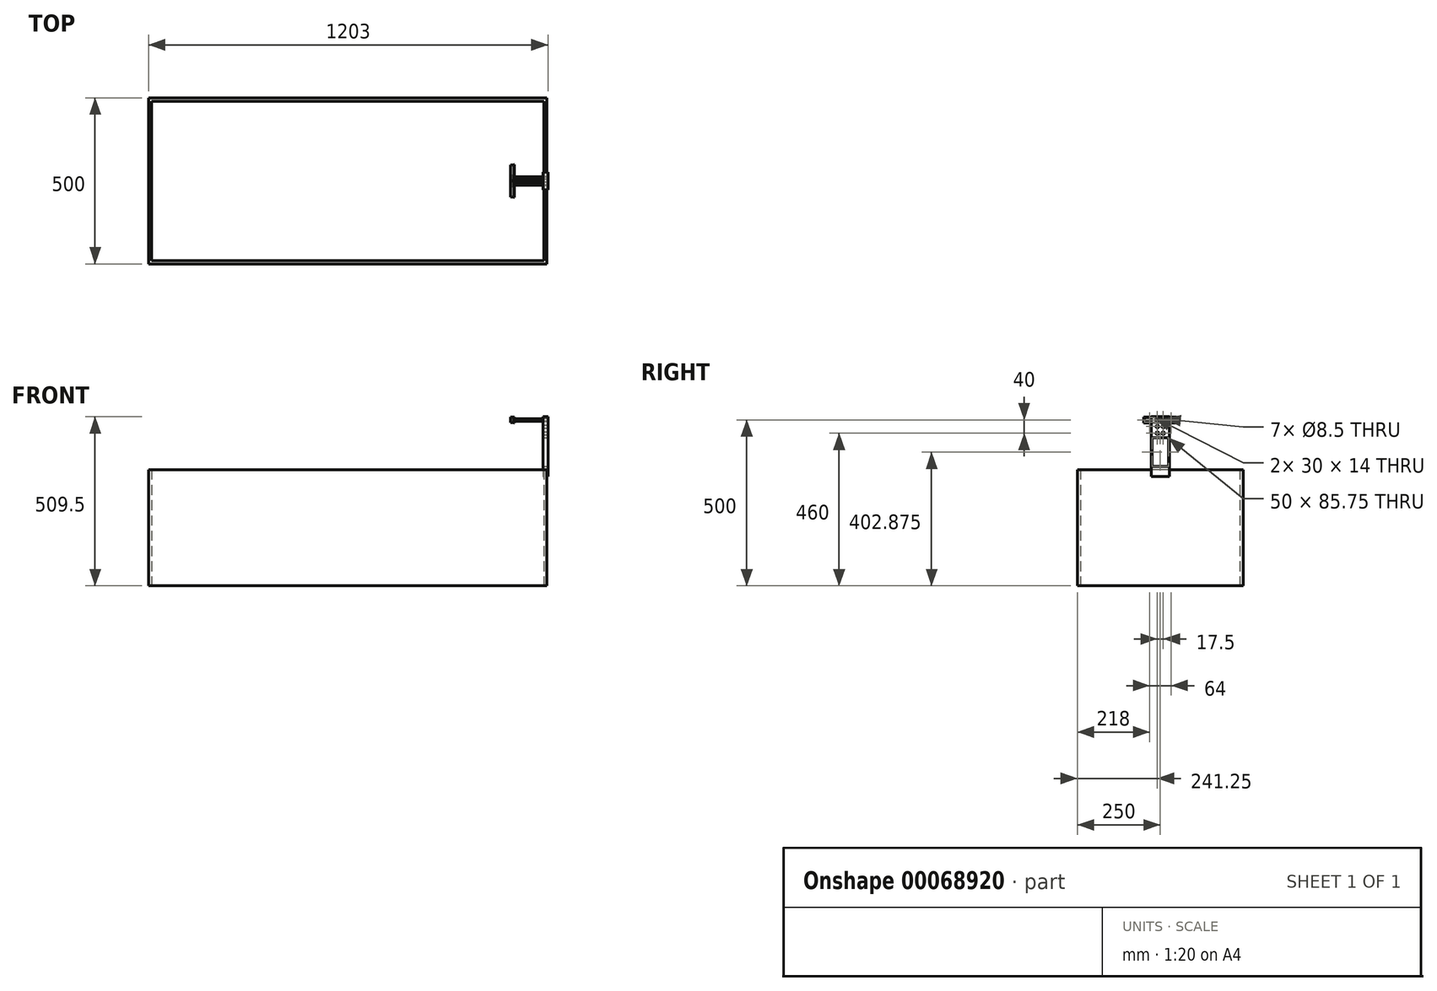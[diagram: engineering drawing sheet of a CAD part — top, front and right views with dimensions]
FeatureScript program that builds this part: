
annotation { "Feature Type Name" : "Feature", "Feature Type Description" : "" }
export const myFeature = defineFeature(function(context is Context, id is Id, definition is map)
    precondition{}
    {
        {
            var Q0;
            Q0=qCreatedBy(makeId("Right.planeOp"),FACE);
            var sketch = newSketch(context, id + "F0", { "sketchPlane" : qUnion([Q0])});
            skLineSegment(sketch, "E0.rect.bottom", {"start": v(-49.5, 9) * mm, "end": v(49.5, 9) * mm});
            skLineSegment(sketch, "E0.rect.top", {"start": v(-49.5, -9) * mm, "end": v(49.5, -9) * mm});
            skLineSegment(sketch, "E0.rect.left", {"start": v(-49.5, 9) * mm, "end": v(-49.5, -9) * mm});
            skLineSegment(sketch, "E0.rect.right", {"start": v(49.5, 9) * mm, "end": v(49.5, -9) * mm});
            skLineSegment(sketch, "E1.bottom", {"start": v(-49.5, -9) * mm, "end": v(0, -9) * mm, "construction": true});
            skLineSegment(sketch, "E1.top", {"start": v(-49.5, 9) * mm, "end": v(0, 9) * mm, "construction": true});
            skLineSegment(sketch, "E2", {"start": v(0, 9) * mm, "end": v(0, -9) * mm, "construction": true});
            skPoint(sketch, "E3.middle", {"position": v(0, 0) * mm});
            skLineSegment(sketch, "E4.bottom", {"start": v(-48, 8) * mm, "end": v(-16, 8) * mm});
            skLineSegment(sketch, "E4.top", {"start": v(-48, -8) * mm, "end": v(-16, -8) * mm});
            skLineSegment(sketch, "E4.left", {"start": v(-48, 8) * mm, "end": v(-48, -8) * mm});
            skLineSegment(sketch, "E5.MirrorCS", {"start": v(48, 8) * mm, "end": v(48, -8) * mm});
            skLineSegment(sketch, "E6.MirrorCS", {"start": v(48, 8) * mm, "end": v(16, 8) * mm});
            skLineSegment(sketch, "E7.MirrorCS", {"start": v(48, -8) * mm, "end": v(16, -8) * mm});
            skLineSegment(sketch, "E8.bottom", {"start": v(50, 9.5) * mm, "end": v(-50, 9.5) * mm});
            skLineSegment(sketch, "E8.top", {"start": v(50, -9.5) * mm, "end": v(-50, -9.5) * mm});
            skLineSegment(sketch, "E8.left", {"start": v(50, 9.5) * mm, "end": v(50, -9.5) * mm});
            skLineSegment(sketch, "E8.right", {"start": v(-50, 9.5) * mm, "end": v(-50, -9.5) * mm});
            skCircle(sketch, "E9", {"center": v(-8.75, 0) * mm, "radius": 4.25 * mm});
            skCircle(sketch, "E10.MirrorC", {"center": v(8.75, 0) * mm, "radius": 4.25 * mm});
            skLineSegment(sketch, "E11.bottom", {"start": v(0.75, 9.5) * mm, "end": v(-0.75, 9.5) * mm});
            skLineSegment(sketch, "E11.top", {"start": v(0.75, -9.5) * mm, "end": v(-0.75, -9.5) * mm});
            skLineSegment(sketch, "E11.left", {"start": v(0.75, 9.5) * mm, "end": v(0.75, -9.5) * mm});
            skLineSegment(sketch, "E11.right", {"start": v(-0.75, 9.5) * mm, "end": v(-0.75, -9.5) * mm});
            skLineSegment(sketch, "E12.0", {"start": v(47, 7) * mm, "end": v(17, 7) * mm});
            skLineSegment(sketch, "E12.1", {"start": v(47, 7) * mm, "end": v(47, -7) * mm});
            skLineSegment(sketch, "E12.2", {"start": v(47, -7) * mm, "end": v(17, -7) * mm});
            skLineSegment(sketch, "E12.3", {"start": v(17, 7) * mm, "end": v(17, -7) * mm});
            skLineSegment(sketch, "E13.MirrorCS", {"start": v(-47, 7) * mm, "end": v(-17, 7) * mm});
            skLineSegment(sketch, "E14.MirrorCS", {"start": v(-17, 7) * mm, "end": v(-17, -7) * mm});
            skLineSegment(sketch, "E15.MirrorCS", {"start": v(-47, -7) * mm, "end": v(-17, -7) * mm});
            skLineSegment(sketch, "E16.MirrorCS", {"start": v(-47, 7) * mm, "end": v(-47, -7) * mm});
            skLineSegment(sketch, "E17.bottom", {"start": v(-13, -8) * mm, "end": v(13, -8) * mm});
            skLineSegment(sketch, "E17.top", {"start": v(-13, 8) * mm, "end": v(13, 8) * mm});
            skLineSegment(sketch, "E18", {"start": v(-16, -8) * mm, "end": v(-13, -8) * mm});
            skLineSegment(sketch, "E19", {"start": v(-16, 8) * mm, "end": v(-13, 8) * mm});
            skLineSegment(sketch, "E20", {"start": v(13, -8) * mm, "end": v(16, -8) * mm});
            skLineSegment(sketch, "E21", {"start": v(13, 8) * mm, "end": v(16, 8) * mm});
            skPoint(sketch, "E3.left.end.orphan", {"position": v(-13, -6) * mm});
            skPoint(sketch, "E22.trimOffspring.start.orphan", {"position": v(-13, 6) * mm});
            skPoint(sketch, "E3.right.end.orphan", {"position": v(13, -6) * mm});
            skPoint(sketch, "E3.right.start.orphan", {"position": v(13, 6) * mm});
            skSolve(sketch);
        }
        {
            var Q0;
            Q0=makeQuery(id+"F0.imprint","IMPRINT",FACE,{"disambiguationData":[TD([[makeQuery(id+"F0.imprint","IMPRINT",EDGE,{"derivedFrom":sQuery(id+"F0.wireOp",EDGE,"E0.rect.bottom")}),-1.0]])]});
            var Q1;
            Q1=makeQuery(id+"F0.imprint","IMPRINT",FACE,{"disambiguationData":[TD([[makeQuery(id+"F0.imprint","IMPRINT",EDGE,{"derivedFrom":sQuery(id+"F0.wireOp",EDGE,"E3.bottom")}),-1.0]])]});
            var Q2;
            {var subQ0=sQuery(id+"F0.wireOp",EDGE,"E11.right");var subQ1=sQuery(id+"F0.wireOp",EDGE,"E0.rect.top");var subQ2=makeQuery(id+"F0.imprint","INTERSECT",VERTEX,{"derivedFrom":[subQ1,subQ0]});Q2=makeQuery(id+"F0.imprint","IMPRINT",FACE,{"disambiguationData":[TD([[makeQuery(id+"F0.imprint","IMPRINT",EDGE,{"disambiguationData":[TD([[subQ2,-1.0]])],"derivedFrom":subQ1}),1.0]])]});}
            var Q3;
            {var subQ4=sQuery(id+"F0.wireOp",EDGE,"E0.rect.right");Q3=makeQuery(id+"F0.imprint","IMPRINT",FACE,{"disambiguationData":[TD([[makeQuery(id+"F0.imprint","IMPRINT",EDGE,{"derivedFrom":subQ4}),-1.0]])]});}
            var Q4;
            {var subQ0=sQuery(id+"F0.wireOp",EDGE,"E3.right");Q4=makeQuery(id+"F0.imprint","IMPRINT",FACE,{"disambiguationData":[TD([[makeQuery(id+"F0.imprint","IMPRINT",EDGE,{"derivedFrom":subQ0}),-1.0]])]});}
            var Q5;
            {var subQ5=sQuery(id+"F0.wireOp",EDGE,"E3.left");Q5=makeQuery(id+"F0.imprint","IMPRINT",FACE,{"disambiguationData":[TD([[makeQuery(id+"F0.imprint","IMPRINT",EDGE,{"derivedFrom":subQ5}),1.0]])]});}
            var Q6;
            {var subQ0=sQuery(id+"F0.wireOp",EDGE,"E0.rect.left");Q6=makeQuery(id+"F0.imprint","IMPRINT",FACE,{"disambiguationData":[TD([[makeQuery(id+"F0.imprint","IMPRINT",EDGE,{"derivedFrom":subQ0}),1.0]])]});}
            var Q7;
            {var subQ0=sQuery(id+"F0.wireOp",EDGE,"E17.top");var subQ1=sQuery(id+"F0.wireOp",EDGE,"E11.left");var subQ2=makeQuery(id+"F0.imprint","INTERSECT",VERTEX,{"derivedFrom":[subQ1,subQ0]});Q7=makeQuery(id+"F0.imprint","IMPRINT",FACE,{"disambiguationData":[TD([[makeQuery(id+"F0.imprint","IMPRINT",EDGE,{"disambiguationData":[TD([[subQ2,-1.0]])],"derivedFrom":subQ1}),-1.0]])]});}
            var Q8;
            Q8=makeQuery(id+"F0.imprint","IMPRINT",FACE,{"disambiguationData":[TD([[makeQuery(id+"F0.imprint","IMPRINT",EDGE,{"derivedFrom":sQuery(id+"F0.wireOp",EDGE,"E10.MirrorC")}),1.0]])]});
            extrude(context, id + "F1", {"entities" : qUnion([Q0, Q1, Q2, Q3, Q4, Q5, Q6, Q7, Q8]), "depth" : 2 * mm});
        }
        {
            var Q0;
            Q0=makeQuery(id+"F0.imprint","IMPRINT",FACE,{"disambiguationData":[TD([[makeQuery(id+"F0.imprint","IMPRINT",EDGE,{"derivedFrom":sQuery(id+"F0.wireOp",EDGE,"E4.bottom")}),-1.0]])]});
            var Q1;
            Q1=makeQuery(id+"F0.imprint","IMPRINT",FACE,{"disambiguationData":[TD([[makeQuery(id+"F0.imprint","IMPRINT",EDGE,{"derivedFrom":sQuery(id+"F0.wireOp",EDGE,"E5.MirrorCS")}),-1.0]])]});
            var Q2;
            {var subQ0=sQuery(id+"F0.wireOp",EDGE,"E3.right");Q2=makeQuery(id+"F0.imprint","IMPRINT",FACE,{"disambiguationData":[TD([[makeQuery(id+"F0.imprint","IMPRINT",EDGE,{"derivedFrom":subQ0}),-1.0]])]});}
            var Q3;
            {var subQ5=sQuery(id+"F0.wireOp",EDGE,"E3.left");Q3=makeQuery(id+"F0.imprint","IMPRINT",FACE,{"disambiguationData":[TD([[makeQuery(id+"F0.imprint","IMPRINT",EDGE,{"derivedFrom":subQ5}),1.0]])]});}
            var Q4;
            Q4=makeQuery(id+"F0.imprint","IMPRINT",FACE,{"disambiguationData":[TD([[makeQuery(id+"F0.imprint","IMPRINT",EDGE,{"derivedFrom":sQuery(id+"F0.wireOp",EDGE,"E10.MirrorC")}),1.0]])]});
            extrude(context, id + "F2", {"entities" : qUnion([Q0, Q1, Q2, Q3, Q4]), "operationType" : NewBodyOperationType.ADD, "oppositeDirection" : true, "depth" : 10 * mm, "hasSecondDirection" : true, "secondDirectionOppositeDirection" : false, "secondDirectionDepth" : 2 * mm});
        }
        {
            var Q0;
            Q0=qSketchRegion(id+"F0",true);
            var Q1;
            Q1=sQuery(id+"F0.wireOp",EDGE,"E8.right");
            var Q2;
            Q2=sQuery(id+"F0.wireOp",EDGE,"E8.top");
            var Q3;
            Q3=sQuery(id+"F0.wireOp",EDGE,"E8.left");
            var Q4;
            Q4=sQuery(id+"F0.wireOp",EDGE,"E8.bottom");
            extrude(context, id + "F3", {"entities" : qUnion([Q0]), "bodyType" : ToolBodyType.SURFACE, "surfaceEntities" : qUnion([Q1, Q2, Q3, Q4]), "oppositeDirection" : true, "depth" : 1000 * mm});
        }
        {
            var Q0;
            Q0=qCreatedBy(makeId("Top.planeOp"),FACE);
            cPlane(context, id + "F4", {"entities" : qUnion([Q0]), "cplaneType" : CPlaneType.OFFSET, "offset" : 500 * mm, "oppositeDirection" : true, "width" : 150 * mm, "height" : 150 * mm});
        }
        {
            var Q0;
            Q0=qCreatedBy(id+"F4.planeOp",FACE);
            var sketch = newSketch(context, id + "F5", { "sketchPlane" : qUnion([Q0])});
            skLineSegment(sketch, "E23.0", {"start": v(-1100, 250) * mm, "end": v(100, 250) * mm});
            skLineSegment(sketch, "E24.0", {"start": v(-1090, 240) * mm, "end": v(-1090, -240) * mm});
            skLineSegment(sketch, "E25.0", {"start": v(-1100, 250) * mm, "end": v(-1100, -250) * mm});
            skLineSegment(sketch, "E26.0", {"start": v(-1100, -250) * mm, "end": v(100, -250) * mm});
            skLineSegment(sketch, "E27.0", {"start": v(-1090, -240) * mm, "end": v(90, -240) * mm});
            skLineSegment(sketch, "E28.0", {"start": v(100, 250) * mm, "end": v(100, -250) * mm});
            skLineSegment(sketch, "E29.0", {"start": v(90, 240) * mm, "end": v(90, -240) * mm});
            skLineSegment(sketch, "E30.0", {"start": v(-1090, 240) * mm, "end": v(90, 240) * mm});
            skSolve(sketch);
        }
        {
            var Q0;
            Q0=qSketchRegion(id+"F5",true);
            extrude(context, id + "F6", {"entities" : qUnion([Q0]), "depth" : 350 * mm});
        }
        {
            var Q0;
            Q0=makeQuery(id+"F6.opExtrude","SWEPT_FACE",FACE,{"disambiguationData":[OSD([sQuery(id+"F5.wireOp",EDGE,"E28.0")])]});
            var sketch = newSketch(context, id + "F7", { "sketchPlane" : qUnion([Q0])});
            skLineSegment(sketch, "E31", {"start": v(0, 0) * mm, "end": v(0, -150) * mm, "construction": true});
            skLineSegment(sketch, "E32", {"start": v(0, -150) * mm, "end": v(0, -500) * mm, "construction": true});
            skLineSegment(sketch, "E33.0", {"start": v(-49.5, -9) * mm, "end": v(49.5, -9) * mm});
            skSolve(sketch);
        }
        {
            var Q0;
            Q0=makeQuery(id+"F6.opExtrude","CAP_FACE",FACE,{"disambiguationData":[OSD([sQuery(id+"F5.wireOp",EDGE,"E23.0"),sQuery(id+"F5.wireOp",EDGE,"E24.0"),sQuery(id+"F5.wireOp",EDGE,"E25.0"),sQuery(id+"F5.wireOp",EDGE,"E26.0"),sQuery(id+"F5.wireOp",EDGE,"E27.0"),sQuery(id+"F5.wireOp",EDGE,"E28.0"),sQuery(id+"F5.wireOp",EDGE,"E29.0"),sQuery(id+"F5.wireOp",EDGE,"E30.0")])],"isStart":false});
            var sketch = newSketch(context, id + "F8", { "sketchPlane" : qUnion([Q0])});
            skLineSegment(sketch, "E34", {"start": v(0, 25) * mm, "end": v(90, 25) * mm, "construction": true});
            skLineSegment(sketch, "E35", {"start": v(0, -25) * mm, "end": v(90, -25) * mm, "construction": true});
            skLineSegment(sketch, "E36.bottom", {"start": v(90, 25) * mm, "end": v(101, 25) * mm});
            skLineSegment(sketch, "E36.top", {"start": v(90, -25) * mm, "end": v(101, -25) * mm});
            skLineSegment(sketch, "E36.left", {"start": v(90, 25) * mm, "end": v(90, -25) * mm});
            skLineSegment(sketch, "E36.right", {"start": v(101, 25) * mm, "end": v(101, -25) * mm});
            skLineSegment(sketch, "E37.0", {"start": v(88, 27) * mm, "end": v(103, 27) * mm});
            skLineSegment(sketch, "E37.1", {"start": v(88, 27) * mm, "end": v(88, -27) * mm});
            skLineSegment(sketch, "E37.2", {"start": v(88, -27) * mm, "end": v(103, -27) * mm});
            skLineSegment(sketch, "E37.3", {"start": v(103, 27) * mm, "end": v(103, -27) * mm});
            skLineSegment(sketch, "E38", {"start": v(90, 25) * mm, "end": v(90, 27) * mm});
            skLineSegment(sketch, "E39", {"start": v(101, 25) * mm, "end": v(101, 27) * mm});
            skLineSegment(sketch, "E40", {"start": v(90, -25) * mm, "end": v(90, -27) * mm});
            skLineSegment(sketch, "E41", {"start": v(101, -25) * mm, "end": v(101, -27) * mm});
            skLineSegment(sketch, "E42", {"start": v(0, 0) * mm, "end": v(105.96, 0) * mm, "construction": true});
            skLineSegment(sketch, "E43", {"start": v(103, 0) * mm, "end": v(88, 0) * mm, "construction": true});
            skSolve(sketch);
        }
        {
            var Q0;
            Q0=makeQuery(id+"F8.imprint","IMPRINT",FACE,{"disambiguationData":[TD([[makeQuery(id+"F8.imprint","IMPRINT",EDGE,{"derivedFrom":sQuery(id+"F8.wireOp",EDGE,"E36.right")}),1.0]])]});
            var Q1;
            Q1=makeQuery(id+"F8.imprint","IMPRINT",FACE,{"disambiguationData":[TD([[makeQuery(id+"F8.imprint","IMPRINT",EDGE,{"derivedFrom":sQuery(id+"F8.wireOp",EDGE,"E36.left")}),-1.0]])]});
            var Q2;
            {var subQ0=sQuery(id+"F8.wireOp",EDGE,"E38");Q2=makeQuery(id+"F8.imprint","IMPRINT",FACE,{"disambiguationData":[TD([[makeQuery(id+"F8.imprint","IMPRINT",EDGE,{"derivedFrom":subQ0}),1.0]])]});}
            var Q3;
            {var subQ0=sQuery(id+"F8.wireOp",EDGE,"E39");Q3=makeQuery(id+"F8.imprint","IMPRINT",FACE,{"disambiguationData":[TD([[makeQuery(id+"F8.imprint","IMPRINT",EDGE,{"derivedFrom":subQ0}),1.0]])]});}
            var Q4;
            {var subQ0=sQuery(id+"F8.wireOp",EDGE,"E41");Q4=makeQuery(id+"F8.imprint","IMPRINT",FACE,{"disambiguationData":[TD([[makeQuery(id+"F8.imprint","IMPRINT",EDGE,{"derivedFrom":subQ0}),-1.0]])]});}
            var Q5;
            {var subQ0=sQuery(id+"F8.wireOp",EDGE,"E40");Q5=makeQuery(id+"F8.imprint","IMPRINT",FACE,{"disambiguationData":[TD([[makeQuery(id+"F8.imprint","IMPRINT",EDGE,{"derivedFrom":subQ0}),1.0]])]});}
            var Q6;
            {var subQ0=sQuery(id+"F8.wireOp",EDGE,"E36.right");Q6=makeQuery(id+"F8.imprint","IMPRINT",FACE,{"disambiguationData":[TD([[makeQuery(id+"F8.imprint","IMPRINT",EDGE,{"derivedFrom":subQ0}),-1.0]])]});}
            var Q7;
            {var subQ0=sQuery(id+"F8.wireOp",EDGE,"E36.left");Q7=makeQuery(id+"F8.imprint","IMPRINT",FACE,{"disambiguationData":[TD([[makeQuery(id+"F8.imprint","IMPRINT",EDGE,{"derivedFrom":subQ0}),1.0]])]});}
            extrude(context, id + "F9", {"entities" : qUnion([Q0, Q1, Q2, Q3, Q4, Q5, Q6, Q7]), "depth" : 10 * mm});
        }
        {
            var Q0;
            Q0=makeQuery(id+"F8.imprint","IMPRINT",FACE,{"disambiguationData":[TD([[makeQuery(id+"F8.imprint","IMPRINT",EDGE,{"derivedFrom":sQuery(id+"F8.wireOp",EDGE,"E36.left")}),-1.0]])]});
            var Q1;
            Q1=makeQuery(id+"F8.imprint","IMPRINT",FACE,{"disambiguationData":[TD([[makeQuery(id+"F8.imprint","IMPRINT",EDGE,{"derivedFrom":sQuery(id+"F8.wireOp",EDGE,"E36.right")}),1.0]])]});
            extrude(context, id + "F10", {"entities" : qUnion([Q0, Q1]), "operationType" : NewBodyOperationType.ADD, "oppositeDirection" : true, "depth" : 20 * mm});
        }
        {
            var Q0;
            {var subQ0=sQuery(id+"F8.wireOp",EDGE,"E37.3");Q0=makeQuery(id+"F10.boolean.opBoolean","MERGE",FACE,{"derivedFrom":[makeQuery(id+"F9.opExtrude","SWEPT_FACE",FACE,{"disambiguationData":[OSD([subQ0])]}),makeQuery(id+"F10.opExtrude","SWEPT_FACE",FACE,{"disambiguationData":[OSD([subQ0])]})]});}
            var sketch = newSketch(context, id + "F11", { "sketchPlane" : qUnion([Q0])});
            skLineSegment(sketch, "E44.0", {"start": v(-27, -140) * mm, "end": v(-27, -170) * mm});
            skLineSegment(sketch, "E45.0", {"start": v(27, -140) * mm, "end": v(27, -170) * mm});
            skLineSegment(sketch, "E46.0", {"start": v(27, -140) * mm, "end": v(-27, -140) * mm});
            skLineSegment(sketch, "E47.0", {"start": v(27, -150) * mm, "end": v(-27, -150) * mm});
            skCircle(sketch, "E48.0", {"center": v(-8.75, 0) * mm, "radius": 4.25 * mm});
            skCircle(sketch, "E49.0", {"center": v(8.75, 0) * mm, "radius": 4.25 * mm});
            skLineSegment(sketch, "E50.bottom", {"start": v(-27, -140) * mm, "end": v(27, -140) * mm});
            skLineSegment(sketch, "E50.top", {"start": v(-27, 9.5) * mm, "end": v(27, 9.5) * mm});
            skLineSegment(sketch, "E50.left", {"start": v(-27, -140) * mm, "end": v(-27, 9.5) * mm});
            skLineSegment(sketch, "E50.right", {"start": v(27, -140) * mm, "end": v(27, 9.5) * mm});
            skLineSegment(sketch, "E51", {"start": v(-8.98, -10) * mm, "end": v(11.55, -10) * mm, "construction": true});
            skCircle(sketch, "E52.MirrorC", {"center": v(-8.75, -20) * mm, "radius": 4.25 * mm});
            skCircle(sketch, "E53.MirrorC", {"center": v(8.75, -20) * mm, "radius": 4.25 * mm});
            skLineSegment(sketch, "E54", {"start": v(-8.28, -30) * mm, "end": v(12.94, -30) * mm});
            skCircle(sketch, "E55.MirrorC", {"center": v(8.75, -40) * mm, "radius": 4.25 * mm});
            skCircle(sketch, "E56.MirrorC", {"center": v(-8.75, -40) * mm, "radius": 4.25 * mm});
            skLineSegment(sketch, "E57.bottom", {"start": v(-25, -54.25) * mm, "end": v(25, -54.25) * mm});
            skLineSegment(sketch, "E57.top", {"start": v(-25, -140) * mm, "end": v(25, -140) * mm});
            skLineSegment(sketch, "E57.left", {"start": v(-25, -54.25) * mm, "end": v(-25, -140) * mm});
            skLineSegment(sketch, "E57.right", {"start": v(25, -54.25) * mm, "end": v(25, -140) * mm});
            skLineSegment(sketch, "E58.0", {"start": v(50, 9.5) * mm, "end": v(-50, 9.5) * mm});
            skLineSegment(sketch, "E59.0", {"start": v(-49.5, -9) * mm, "end": v(49.5, -9) * mm, "construction": true});
            skLineSegment(sketch, "E60.0", {"start": v(250, -150) * mm, "end": v(-250, -150) * mm, "construction": true});
            skSolve(sketch);
        }
        {
            var Q0;
            Q0=qSketchRegion(id+"F11",true);
            var Q1;
            Q1=makeQuery(id+"F11.imprint","IMPRINT",FACE,{"disambiguationData":[TD([[makeQuery(id+"F11.imprint","IMPRINT",EDGE,{"derivedFrom":sQuery(id+"F11.wireOp",EDGE,"E48.0")}),-1.0]])]});
            extrude(context, id + "F12", {"entities" : qUnion([Q0, Q1]), "operationType" : NewBodyOperationType.ADD, "oppositeDirection" : true, "depth" : 15 * mm});
        }
        {
            var Q0;
            Q0=qCreatedBy(makeId("Top.planeOp"),FACE);
            var sketch = newSketch(context, id + "F13", { "sketchPlane" : qUnion([Q0])});
            skLineSegment(sketch, "E61.bottom", {"start": v(-7, -4.5) * mm, "end": v(103, -4.5) * mm});
            skLineSegment(sketch, "E61.top", {"start": v(-7, -8.5) * mm, "end": v(103, -8.5) * mm});
            skLineSegment(sketch, "E61.left", {"start": v(-7, -4.5) * mm, "end": v(-7, -8.5) * mm});
            skLineSegment(sketch, "E61.right", {"start": v(103, -4.5) * mm, "end": v(103, -8.5) * mm});
            skLineSegment(sketch, "E62", {"start": v(0, 0) * mm, "end": v(122.29, 0) * mm, "construction": true});
            skLineSegment(sketch, "E63.MirrorCS", {"start": v(-7, 4.5) * mm, "end": v(-7, 8.5) * mm});
            skLineSegment(sketch, "E64.MirrorCS", {"start": v(103, 4.5) * mm, "end": v(103, 8.5) * mm});
            skLineSegment(sketch, "E65.MirrorCS", {"start": v(-7, 8.5) * mm, "end": v(103, 8.5) * mm});
            skLineSegment(sketch, "E66.MirrorCS", {"start": v(-7, 4.5) * mm, "end": v(103, 4.5) * mm});
            skLineSegment(sketch, "E67.0", {"start": v(103, 4.5) * mm, "end": v(103, 13) * mm});
            skLineSegment(sketch, "E68.0", {"start": v(103, -4.5) * mm, "end": v(103, -13) * mm});
            skSolve(sketch);
        }
        {
            var Q0;
            Q0=makeQuery(id+"F13.imprint","IMPRINT",FACE,{"disambiguationData":[TD([[makeQuery(id+"F13.imprint","IMPRINT",EDGE,{"derivedFrom":sQuery(id+"F13.wireOp",EDGE,"E61.bottom")}),-1.0]])]});
            var Q1;
            Q1=sQuery(id+"F13.wireOp",EDGE,"E61.top");
            revolve(context, id + "F14", {"entities" : qUnion([Q0]), "axis" : qUnion([Q1]), "revolveType" : RevolveType.FULL});
        }
        {
            var Q0;
            Q0=makeQuery(id+"F13.imprint","IMPRINT",FACE,{"disambiguationData":[TD([[makeQuery(id+"F13.imprint","IMPRINT",EDGE,{"derivedFrom":sQuery(id+"F13.wireOp",EDGE,"E64.MirrorCS")}),1.0]])]});
            var Q1;
            {var subQ0=sQuery(id+"F13.wireOp",EDGE,"E63.MirrorCS");Q1=makeQuery(id+"F13.imprint","IMPRINT",FACE,{"disambiguationData":[TD([[makeQuery(id+"F13.imprint","IMPRINT",EDGE,{"derivedFrom":subQ0}),-1.0]])]});}
            var Q2;
            Q2=sQuery(id+"F13.wireOp",EDGE,"E65.MirrorCS");
            revolve(context, id + "F15", {"entities" : qUnion([Q0, Q1]), "axis" : qUnion([Q2]), "revolveType" : RevolveType.FULL});
        }
    });
